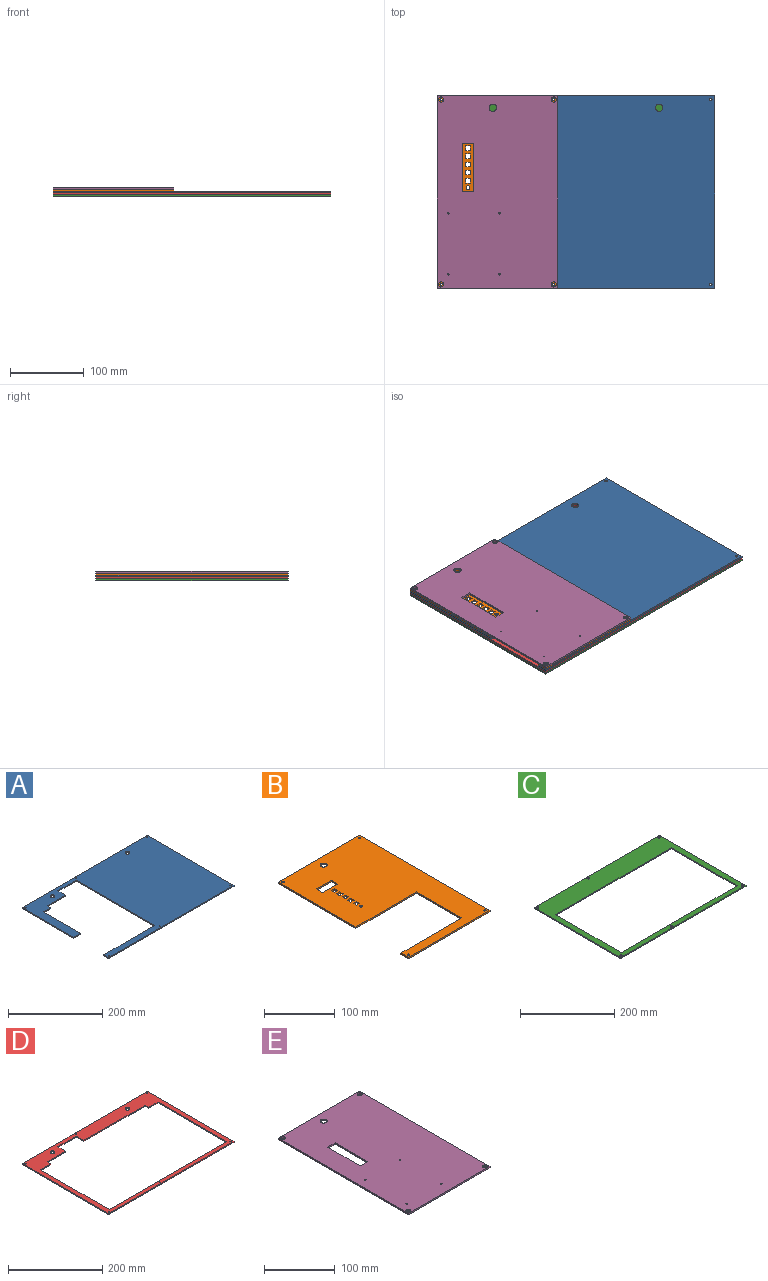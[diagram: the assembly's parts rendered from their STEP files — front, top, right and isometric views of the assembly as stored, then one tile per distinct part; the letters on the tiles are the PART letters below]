
ASSEMBLY  parts=5 mates=4
PART A: 24 faces, bbox 375x260x2.5 mm
  f0: plane 21.5x2.5mm, normal (0,-1,0), area 53.7mm2, adj f1,f20,f22,f23
  f1: plane 111x2.5mm, normal (1,0,0), area 277.5mm2, adj f0,f2,f22,f23
  f2: plane 21x2.5mm, normal (0,-1,0), area 52.5mm2, adj f1,f3,f22,f23
  f3: plane 11x2.5mm, normal (1,0,0), area 27.5mm2, adj f2,f4,f22,f23
  f4: plane 55x2.5mm, normal (0,-1,0), area 137.5mm2, adj f3,f5,f22,f23
  f5: plane 23x2.5mm, normal (1,0,0), area 57.5mm2, adj f4,f6,f22,f23
  f6: plane 55x2.5mm, normal (0,-1,0), area 137.5mm2, adj f5,f7,f22,f23
  f7: plane 235x2.5mm, normal (-1,0,0), area 587.5mm2, adj f6,f8,f22,f23
  f8: plane 152.5x2.5mm, normal (0,1,0), area 381.3mm2, adj f7,f9,f22,f23
  f9: plane 15x2.5mm, normal (-1,0,0), area 37.5mm2, adj f8,f10,f22,f23
  f10: plane 375x2.5mm, normal (0,-1,0), area 937.5mm2, adj f9,f11,f22,f23
  f11: plane 260x2.5mm, normal (1,0,0), area 650mm2, adj f10,f12,f22,f23
  f12: plane 375x2.5mm, normal (0,1,0), area 937.5mm2, adj f11,f20,f22,f23
  f13: cylinder r=5mm len=10mm, axis (0,0,-1), area 78.5mm2, adj f22,f23
  f14: cylinder r=1.5mm len=3mm, axis (0,0,-1), area 23.6mm2, adj f22,f23
  f15: cylinder r=1.5mm len=3mm, axis (0,0,-1), area 23.6mm2, adj f22,f23
  f16: cylinder r=1.5mm len=3mm, axis (0,0,-1), area 23.6mm2, adj f22,f23
  f17: cylinder r=1.5mm len=3mm, axis (0,0,-1), area 23.6mm2, adj f22,f23
  f18: cylinder r=1.5mm len=3mm, axis (0,0,-1), area 23.6mm2, adj f22,f23
  f19: cylinder r=1.5mm len=3mm, axis (0,0,-1), area 23.6mm2, adj f22,f23
  f20: plane 155x2.5mm, normal (-1,0,0), area 387.5mm2, adj f0,f12,f22,f23
  f21: cylinder r=5mm len=10mm, axis (0,0,-1), area 78.5mm2, adj f22,f23
  f22: plane 375x260mm, normal (0,0,1), area 66559.5mm2, adj f0,f1,f2,f3,f4,f5,f6,f7
  f23: plane 375x260mm, normal (0,0,-1), area 66559.5mm2, adj f0,f1,f2,f3,f4,f5,f6,f7
PART B: 40 faces, bbox 162.5x260x2.5 mm
  f0: plane 6.5x2.5mm, normal (-1,0,0), area 16.2mm2, adj f1,f37,f38,f39
  f1: plane 6.5x2.5mm, normal (0,1,0), area 16.3mm2, adj f0,f2,f38,f39
  f2: plane 6.5x2.5mm, normal (1,0,0), area 16.2mm2, adj f1,f37,f38,f39
  f3: plane 6.5x2.5mm, normal (0,-1,0), area 16.3mm2, adj f4,f25,f38,f39
  f4: plane 6.5x2.5mm, normal (-1,0,0), area 16.2mm2, adj f3,f5,f38,f39
  f5: plane 6.5x2.5mm, normal (0,1,0), area 16.3mm2, adj f4,f25,f38,f39
  f6: plane 6.5x2.5mm, normal (0,-1,0), area 16.3mm2, adj f7,f26,f38,f39
  f7: plane 6.5x2.5mm, normal (-1,0,0), area 16.2mm2, adj f6,f8,f38,f39
  f8: plane 6.5x2.5mm, normal (0,1,0), area 16.3mm2, adj f7,f26,f38,f39
  f9: plane 6.5x2.5mm, normal (0,-1,0), area 16.3mm2, adj f10,f27,f38,f39
  f10: plane 6.5x2.5mm, normal (-1,0,0), area 16.2mm2, adj f9,f11,f38,f39
  f11: plane 6.5x2.5mm, normal (0,1,0), area 16.3mm2, adj f10,f27,f38,f39
  f12: plane 6.5x2.5mm, normal (0,-1,0), area 16.3mm2, adj f13,f29,f38,f39
  f13: plane 6.5x2.5mm, normal (-1,0,0), area 16.2mm2, adj f12,f14,f38,f39
  f14: plane 6.5x2.5mm, normal (0,1,0), area 16.3mm2, adj f13,f29,f38,f39
  f15: plane 260x2.5mm, normal (1,0,0), area 650mm2, adj f16,f34,f38,f39
  f16: plane 162.5x2.5mm, normal (0,1,0), area 406.2mm2, adj f15,f17,f38,f39
  f17: plane 155x2.5mm, normal (-1,0,0), area 387.5mm2, adj f16,f18,f38,f39
  f18: plane 121.5x2.5mm, normal (0,-1,0), area 303.7mm2, adj f17,f19,f38,f39
  f19: plane 90x2.5mm, normal (-1,0,0), area 225mm2, adj f18,f20,f38,f39
  f20: plane 121.5x2.5mm, normal (0,1,0), area 303.7mm2, adj f19,f21,f38,f39
  f21: plane 15x2.5mm, normal (-1,0,0), area 37.5mm2, adj f20,f34,f38,f39
  f22: plane 13x2.5mm, normal (-1,0,0), area 32.5mm2, adj f23,f36,f38,f39
  f23: plane 30x2.5mm, normal (0,1,0), area 75mm2, adj f22,f24,f38,f39
  f24: plane 13x2.5mm, normal (1,0,0), area 32.5mm2, adj f23,f36,f38,f39
  f25: plane 6.5x2.5mm, normal (1,0,0), area 16.2mm2, adj f3,f5,f38,f39
  f26: plane 6.5x2.5mm, normal (1,0,0), area 16.2mm2, adj f6,f8,f38,f39
  f27: plane 6.5x2.5mm, normal (1,0,0), area 16.2mm2, adj f9,f11,f38,f39
  f28: cylinder r=2.5mm len=5mm, axis (0,0,-1), area 39.3mm2, adj f38,f39
  f29: plane 6.5x2.5mm, normal (1,0,0), area 16.2mm2, adj f12,f14,f38,f39
  f30: cylinder r=1.5mm len=3mm, axis (0,0,-1), area 23.6mm2, adj f38,f39
  f31: cylinder r=1.5mm len=3mm, axis (0,0,-1), area 23.6mm2, adj f38,f39
  f32: cylinder r=1.5mm len=3mm, axis (0,0,-1), area 23.6mm2, adj f38,f39
  f33: cylinder r=1.5mm len=3mm, axis (0,0,-1), area 23.6mm2, adj f38,f39
  f34: plane 162.5x2.5mm, normal (0,-1,0), area 406.2mm2, adj f15,f21,f38,f39
  f35: cylinder r=5mm len=10mm, axis (0,0,-1), area 78.5mm2, adj f38,f39
  f36: plane 30x2.5mm, normal (0,-1,0), area 75mm2, adj f22,f24,f38,f39
  f37: plane 6.5x2.5mm, normal (0,-1,0), area 16.3mm2, adj f0,f2,f38,f39
  f38: plane 260x162.5mm, normal (0,0,1), area 30587.3mm2, adj f0,f1,f2,f3,f4,f5,f6,f7
  f39: plane 260x162.5mm, normal (0,0,-1), area 30587.3mm2, adj f0,f1,f2,f3,f4,f5,f6,f7
PART C: 16 faces, bbox 375x260x2.5 mm
  f0: plane 260x2.5mm, normal (1,0,0), area 650mm2, adj f1,f11,f14,f15
  f1: plane 375x2.5mm, normal (0,1,0), area 937.5mm2, adj f0,f2,f14,f15
  f2: plane 260x2.5mm, normal (-1,0,0), area 650mm2, adj f1,f11,f14,f15
  f3: plane 347x2.5mm, normal (0,-1,0), area 867.5mm2, adj f4,f12,f14,f15
  f4: plane 197x2.5mm, normal (-1,0,0), area 492.5mm2, adj f3,f5,f14,f15
  f5: plane 347x2.5mm, normal (0,1,0), area 867.5mm2, adj f4,f12,f14,f15
  f6: cylinder r=3mm len=6mm, axis (0,0,-1), area 47.1mm2, adj f14,f15
  f7: cylinder r=3mm len=6mm, axis (0,0,-1), area 47.1mm2, adj f14,f15
  f8: cylinder r=3mm len=6mm, axis (0,0,-1), area 47.1mm2, adj f14,f15
  f9: cylinder r=3mm len=6mm, axis (0,0,-1), area 47.1mm2, adj f14,f15
  f10: cylinder r=3mm len=6mm, axis (0,0,-1), area 47.1mm2, adj f14,f15
  f11: plane 375x2.5mm, normal (0,-1,0), area 937.5mm2, adj f0,f2,f14,f15
  f12: plane 197x2.5mm, normal (1,0,0), area 492.5mm2, adj f3,f5,f14,f15
  f13: cylinder r=3mm len=6mm, axis (0,0,-1), area 47.1mm2, adj f14,f15
  f14: plane 375x260mm, normal (0,0,1), area 28971.4mm2, adj f0,f1,f2,f3,f4,f5,f6,f7
  f15: plane 375x260mm, normal (0,0,-1), area 28971.4mm2, adj f0,f1,f2,f3,f4,f5,f6,f7
PART D: 26 faces, bbox 375x260x2.5 mm
  f0: plane 260x2.5mm, normal (1,0,0), area 650mm2, adj f1,f21,f24,f25
  f1: plane 375x2.5mm, normal (0,1,0), area 937.5mm2, adj f0,f2,f24,f25
  f2: plane 260x2.5mm, normal (-1,0,0), area 650mm2, adj f1,f21,f24,f25
  f3: plane 28x2.5mm, normal (0,-1,0), area 70mm2, adj f4,f22,f24,f25
  f4: plane 206x2.5mm, normal (-1,0,0), area 515mm2, adj f3,f5,f24,f25
  f5: plane 352x2.5mm, normal (0,1,0), area 880mm2, adj f4,f6,f24,f25
  f6: plane 206x2.5mm, normal (1,0,0), area 515mm2, adj f5,f7,f24,f25
  f7: plane 31x2.5mm, normal (0,-1,0), area 77.5mm2, adj f6,f8,f24,f25
  f8: plane 11x2.5mm, normal (1,0,0), area 27.5mm2, adj f7,f9,f24,f25
  f9: plane 55x2.5mm, normal (0,-1,0), area 137.5mm2, adj f8,f10,f24,f25
  f10: plane 23x2.5mm, normal (1,0,0), area 57.5mm2, adj f9,f11,f24,f25
  f11: plane 55x2.5mm, normal (0,-1,0), area 137.5mm2, adj f10,f12,f24,f25
  f12: plane 23x2.5mm, normal (-1,0,0), area 57.5mm2, adj f11,f13,f24,f25
  f13: plane 183x2.5mm, normal (0,-1,0), area 457.5mm2, adj f12,f22,f24,f25
  f14: cylinder r=5mm len=10mm, axis (0,0,-1), area 78.5mm2, adj f24,f25
  f15: cylinder r=1.5mm len=3mm, axis (0,0,-1), area 23.6mm2, adj f24,f25
  f16: cylinder r=1.5mm len=3mm, axis (0,0,-1), area 23.6mm2, adj f24,f25
  f17: cylinder r=1.5mm len=3mm, axis (0,0,-1), area 23.6mm2, adj f24,f25
  f18: cylinder r=1.5mm len=3mm, axis (0,0,-1), area 23.6mm2, adj f24,f25
  f19: cylinder r=1.5mm len=3mm, axis (0,0,-1), area 23.6mm2, adj f24,f25
  f20: cylinder r=1.5mm len=3mm, axis (0,0,-1), area 23.6mm2, adj f24,f25
  f21: plane 375x2.5mm, normal (0,-1,0), area 937.5mm2, adj f0,f2,f24,f25
  f22: plane 11x2.5mm, normal (-1,0,0), area 27.5mm2, adj f3,f13,f24,f25
  f23: cylinder r=5mm len=10mm, axis (0,0,-1), area 78.5mm2, adj f24,f25
  f24: plane 375x260mm, normal (0,0,1), area 20300.5mm2, adj f0,f1,f2,f3,f4,f5,f6,f7
  f25: plane 375x260mm, normal (0,0,-1), area 20300.5mm2, adj f0,f1,f2,f3,f4,f5,f6,f7
PART E: 19 faces, bbox 162.5x260x2.5 mm
  f0: plane 15x2.5mm, normal (0,1,0), area 37.5mm2, adj f1,f16,f17,f18
  f1: plane 65x2.5mm, normal (1,0,0), area 162.5mm2, adj f0,f2,f17,f18
  f2: plane 15x2.5mm, normal (0,-1,0), area 37.5mm2, adj f1,f16,f17,f18
  f3: plane 260x2.5mm, normal (-1,0,0), area 650mm2, adj f4,f12,f17,f18
  f4: plane 162.5x2.5mm, normal (0,-1,0), area 406.2mm2, adj f3,f5,f17,f18
  f5: plane 260x2.5mm, normal (1,0,0), area 650mm2, adj f4,f12,f17,f18
  f6: cylinder r=3.5mm len=7mm, axis (0,0,-1), area 55mm2, adj f17,f18
  f7: cylinder r=3.5mm len=7mm, axis (0,0,-1), area 55mm2, adj f17,f18
  f8: cylinder r=5mm len=10mm, axis (0,0,-1), area 78.5mm2, adj f17,f18
  f9: cylinder r=3.5mm len=7mm, axis (0,0,-1), area 55mm2, adj f17,f18
  f10: cylinder r=3.5mm len=7mm, axis (0,0,-1), area 55mm2, adj f17,f18
  f11: cylinder r=1mm len=2.5mm, axis (0,0,-1), area 15.7mm2, adj f17,f18
  f12: plane 162.5x2.5mm, normal (0,1,0), area 406.2mm2, adj f3,f5,f17,f18
  f13: cylinder r=1mm len=2.5mm, axis (0,0,-1), area 15.7mm2, adj f17,f18
  f14: cylinder r=1mm len=2.5mm, axis (0,0,-1), area 15.7mm2, adj f17,f18
  f15: cylinder r=1mm len=2.5mm, axis (0,0,-1), area 15.7mm2, adj f17,f18
  f16: plane 65x2.5mm, normal (-1,0,0), area 162.5mm2, adj f0,f2,f17,f18
  f17: plane 260x162.5mm, normal (0,0,1), area 41030mm2, adj f0,f1,f2,f3,f4,f5,f6,f7
  f18: plane 260x162.5mm, normal (0,0,-1), area 41030mm2, adj f0,f1,f2,f3,f4,f5,f6,f7
PLACE A t=(-15.39,44.49,41.06)mm
PLACE B t=(-15.39,44.49,43.56)mm
PLACE C t=(-15.39,44.49,36.06)mm
PLACE D t=(-15.39,44.49,38.56)mm
PLACE E t=(-15.39,44.49,46.06)mm
MATE fastened C.f11 <-> D.f21  axis (0,-1,0) through (172.11,-85.51,38.56)mm
MATE fastened B.f21 <-> A.f9  axis (-1,0,0) through (-202.89,-85.51,43.56)mm
MATE fastened E.f3 <-> B.f21  axis (-1,0,0) through (-202.89,-85.51,46.06)mm
MATE fastened D.f21 <-> A.f10  axis (0,-1,0) through (172.11,-85.51,41.06)mm
